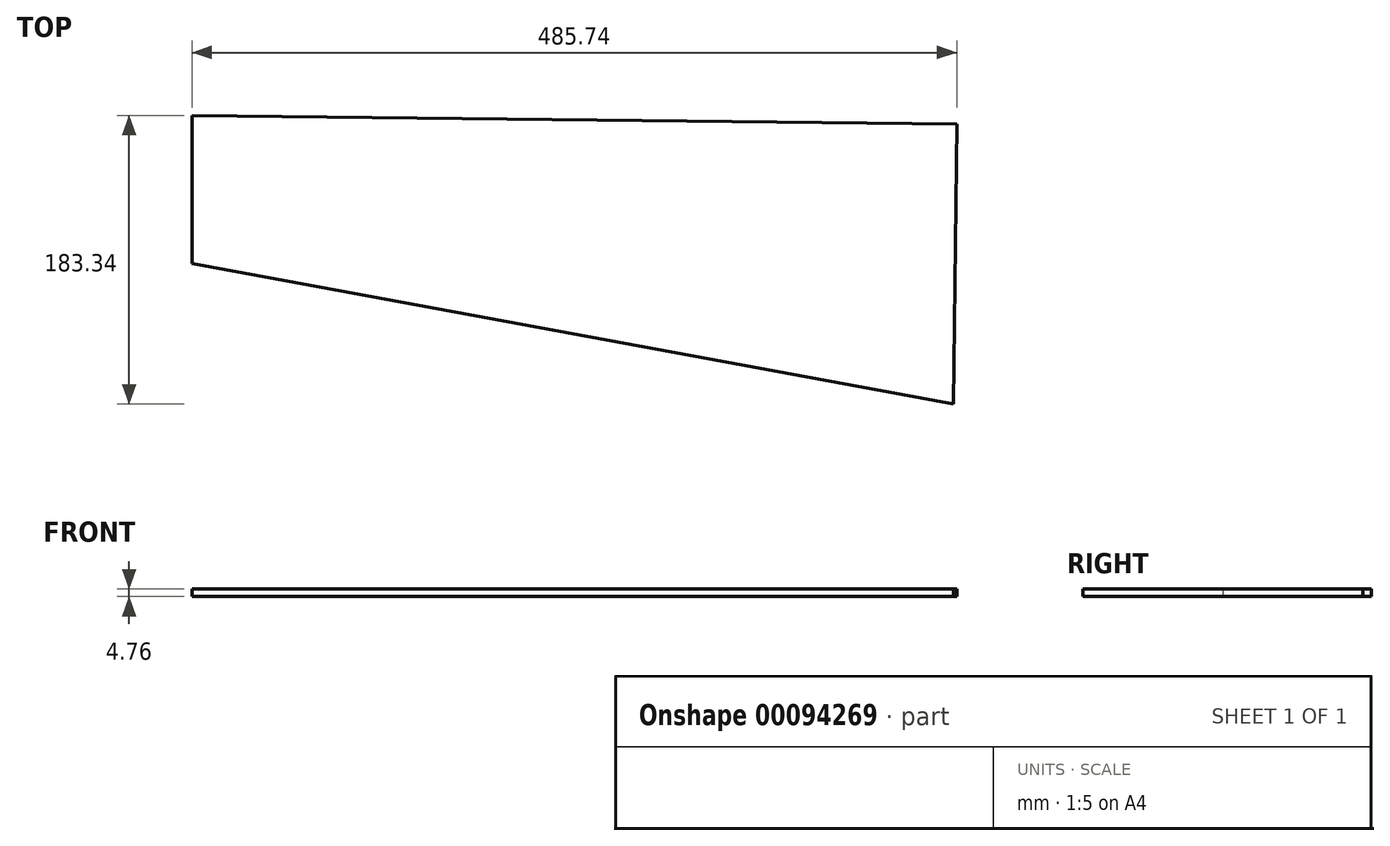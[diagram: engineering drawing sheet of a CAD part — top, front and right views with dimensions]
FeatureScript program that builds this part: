
annotation { "Feature Type Name" : "Feature", "Feature Type Description" : "" }
export const myFeature = defineFeature(function(context is Context, id is Id, definition is map)
    precondition{}
    {
        {
            var Q0;
            Q0=qCreatedBy(makeId("Top.planeOp"),FACE);
            var sketch = newSketch(context, id + "F0", { "sketchPlane" : qUnion([Q0])});
            skLineSegment(sketch, "E0", {"start": v(176.67, -5.74) * mm, "end": v(174.64, -183.52) * mm});
            skLineSegment(sketch, "E1", {"start": v(174.64, -183.52) * mm, "end": v(-324.95, -91.44) * mm});
            skLineSegment(sketch, "E2", {"start": v(-324.95, 0) * mm, "end": v(176.67, -5.74) * mm});
            skLineSegment(sketch, "E3", {"start": v(-309.07, -0.18) * mm, "end": v(-309.07, -94.37) * mm});
            skSolve(sketch);
        }
        {
            var Q0;
            Q0=makeQuery(id+"F0.imprint","IMPRINT",FACE,{"disambiguationData":[TD([[makeQuery(id+"F0.imprint","IMPRINT",EDGE,{"derivedFrom":sQuery(id+"F0.wireOp",EDGE,"E0")}),-1.0]])]});
            extrude(context, id + "F1", {"entities" : qUnion([Q0]), "depth" : 4.76 * mm});
        }
    });
